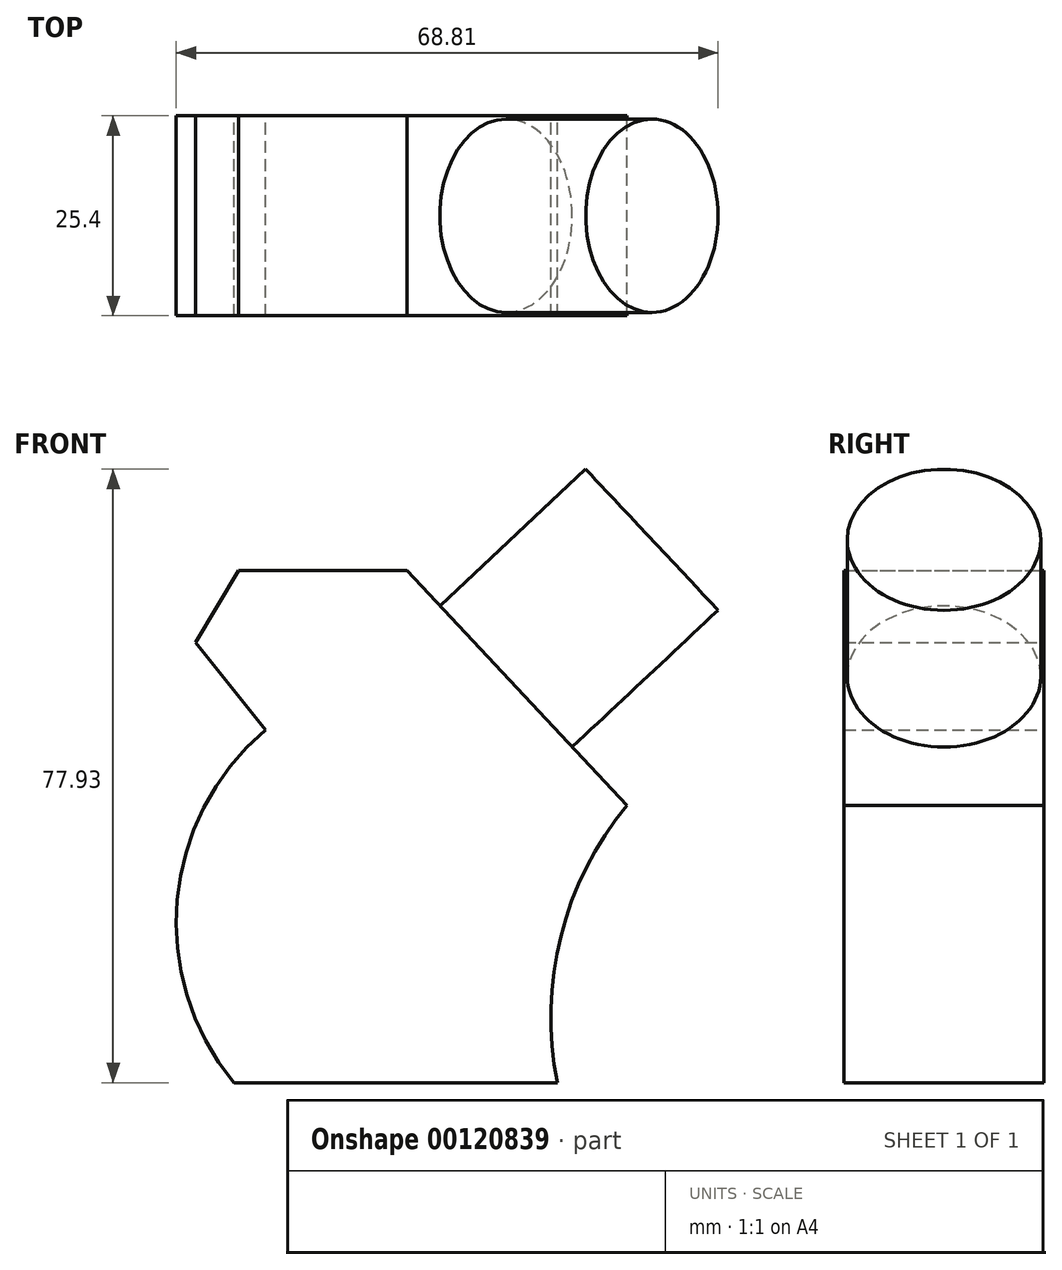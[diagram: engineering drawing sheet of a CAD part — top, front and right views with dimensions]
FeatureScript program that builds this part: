
annotation { "Feature Type Name" : "Feature", "Feature Type Description" : "" }
export const myFeature = defineFeature(function(context is Context, id is Id, definition is map)
    precondition{}
    {
        {
            var Q0;
            Q0=qCreatedBy(makeId("Front.planeOp"),FACE);
            var sketch = newSketch(context, id + "F0", { "sketchPlane" : qUnion([Q0])});
            skLineSegment(sketch, "E0", {"start": v(-17.11, -35.23) * mm, "end": v(23.96, -35.23) * mm});
            skArc(sketch, "E1", {"start": v(32.8, 0) * mm, "mid": v(24.42, -16.62) * mm, "end": v(23.96, -35.23) * mm});
            skLineSegment(sketch, "E2", {"start": v(32.8, 0) * mm, "end": v(4.85, 29.8) * mm});
            skLineSegment(sketch, "E3", {"start": v(4.85, 29.8) * mm, "end": v(-16.54, 29.8) * mm});
            skLineSegment(sketch, "E4", {"start": v(-16.54, 29.8) * mm, "end": v(-21.96, 20.68) * mm});
            skLineSegment(sketch, "E5", {"start": v(-21.96, 20.68) * mm, "end": v(-13.12, 9.56) * mm});
            skArc(sketch, "E6", {"start": v(-13.12, 9.56) * mm, "mid": v(-24.3, -12.02) * mm, "end": v(-17.11, -35.23) * mm});
            skSolve(sketch);
        }
        {
            var Q0;
            Q0=makeQuery(id+"F0.imprint","IMPRINT",FACE,{"disambiguationData":[TD([[makeQuery(id+"F0.imprint","IMPRINT",EDGE,{"derivedFrom":sQuery(id+"F0.wireOp",EDGE,"E0")}),1.0]])]});
            extrude(context, id + "F1", {"entities" : qUnion([Q0]), "depth" : 25.4 * mm});
        }
        {
            var Q0;
            Q0=makeQuery(id+"F1.opExtrude","SWEPT_FACE",FACE,{"disambiguationData":[OSD([sQuery(id+"F0.wireOp",EDGE,"E2")])]});
            var sketch = newSketch(context, id + "F2", { "sketchPlane" : qUnion([Q0])});
            skCircle(sketch, "E7", {"center": v(-12.7, 0) * mm, "radius": 12.29 * mm});
            skSolve(sketch);
        }
        {
            var Q0;
            Q0 = qSketchRegion(id + "F2", true);
            extrude(context, id + "F3", {"entities" : qUnion([Q0]), "operationType" : NewBodyOperationType.ADD, "depth" : 25.4 * mm});
        }
    });
